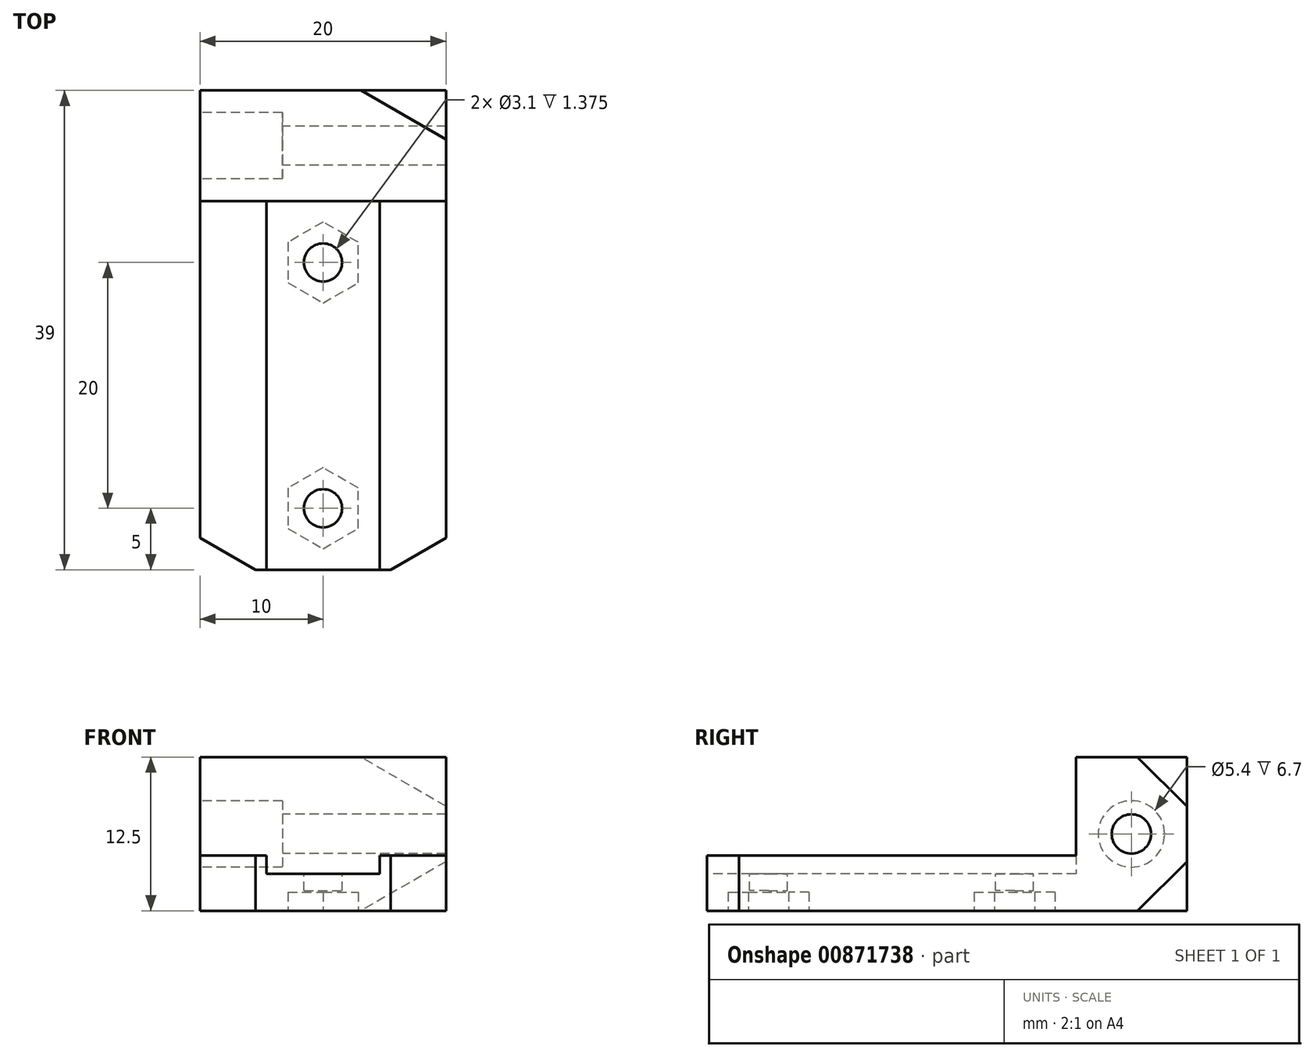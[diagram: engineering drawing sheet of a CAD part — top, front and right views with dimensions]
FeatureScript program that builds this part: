
annotation { "Feature Type Name" : "Feature", "Feature Type Description" : "" }
export const myFeature = defineFeature(function(context is Context, id is Id, definition is map)
    precondition{}
    {
        {
            var Q0;
            Q0=qCreatedBy(makeId("Top.planeOp"),FACE);
            var sketch = newSketch(context, id + "F0", { "sketchPlane" : qUnion([Q0])});
            skLineSegment(sketch, "E0.bottom", {"start": v(10, 19.5) * mm, "end": v(-10, 19.5) * mm});
            skLineSegment(sketch, "E0.top", {"start": v(10, -19.5) * mm, "end": v(-10, -19.5) * mm});
            skLineSegment(sketch, "E0.left", {"start": v(10, 19.5) * mm, "end": v(10, -19.5) * mm});
            skLineSegment(sketch, "E0.right", {"start": v(-10, 19.5) * mm, "end": v(-10, -19.5) * mm});
            skPoint(sketch, "E0.middle", {"position": v(0, 0) * mm});
            skSolve(sketch);
        }
        {
            var Q0;
            Q0=makeQuery(id+"F0.imprint","IMPRINT",FACE,{"disambiguationData":[TD([[makeQuery(id+"F0.imprint","IMPRINT",EDGE,{"derivedFrom":sQuery(id+"F0.wireOp",EDGE,"E0.bottom")}),1.0]])]});
            extrude(context, id + "F1", {"entities" : qUnion([Q0]), "depth" : 3 * mm, "offsetDistance" : 25 * mm});
        }
        {
            var Q0;
            Q0=makeQuery(id+"F1.opExtrude","CAP_FACE",FACE,{"disambiguationData":[OSD([sQuery(id+"F0.wireOp",EDGE,"E0.bottom"),sQuery(id+"F0.wireOp",EDGE,"E0.top"),sQuery(id+"F0.wireOp",EDGE,"E0.left"),sQuery(id+"F0.wireOp",EDGE,"E0.right")])],"isStart":false});
            var sketch = newSketch(context, id + "F2", { "sketchPlane" : qUnion([Q0])});
            skLineSegment(sketch, "E1", {"start": v(-10, -19.5) * mm, "end": v(-4.6, -19.5) * mm});
            skLineSegment(sketch, "E2", {"start": v(-4.6, -19.5) * mm, "end": v(-4.6, 10.5) * mm});
            skLineSegment(sketch, "E3", {"start": v(-4.6, 10.5) * mm, "end": v(4.6, 10.5) * mm});
            skLineSegment(sketch, "E4", {"start": v(4.6, 10.5) * mm, "end": v(4.6, -19.5) * mm});
            skLineSegment(sketch, "E5", {"start": v(4.6, -19.5) * mm, "end": v(10, -19.5) * mm});
            skLineSegment(sketch, "E6", {"start": v(10, -19.5) * mm, "end": v(10, 19.5) * mm});
            skLineSegment(sketch, "E7", {"start": v(10, 19.5) * mm, "end": v(-10, 19.5) * mm});
            skLineSegment(sketch, "E8", {"start": v(-10, 19.5) * mm, "end": v(-10, -19.5) * mm});
            skLineSegment(sketch, "E9", {"start": v(0, 10.5) * mm, "end": v(0, 0) * mm, "construction": true});
            skSolve(sketch);
        }
        {
            var Q0;
            Q0 = qSketchRegion(id + "F2", true);
            extrude(context, id + "F3", {"entities" : qUnion([Q0]), "operationType" : NewBodyOperationType.ADD, "depth" : 1.5 * mm, "offsetDistance" : 25 * mm});
        }
        {
            var Q0;
            Q0=makeQuery(id+"F1.opExtrude","CAP_FACE",FACE,{"disambiguationData":[OSD([sQuery(id+"F0.wireOp",EDGE,"E0.bottom"),sQuery(id+"F0.wireOp",EDGE,"E0.top"),sQuery(id+"F0.wireOp",EDGE,"E0.left"),sQuery(id+"F0.wireOp",EDGE,"E0.right")])],"isStart":false});
            var sketch = newSketch(context, id + "F4", { "sketchPlane" : qUnion([Q0])});
            skLineSegment(sketch, "E10.bottom", {"start": v(-10, 19.5) * mm, "end": v(10, 19.5) * mm});
            skLineSegment(sketch, "E10.top", {"start": v(-10, 10.5) * mm, "end": v(10, 10.5) * mm});
            skLineSegment(sketch, "E10.left", {"start": v(-10, 19.5) * mm, "end": v(-10, 10.5) * mm});
            skLineSegment(sketch, "E10.right", {"start": v(10, 19.5) * mm, "end": v(10, 10.5) * mm});
            skSolve(sketch);
        }
        {
            var Q0;
            Q0 = qSketchRegion(id + "F4", true);
            var Q1;
            Q1=makeQuery(id+"F1.opExtrude","CAP_FACE",FACE,{"disambiguationData":[OSD([sQuery(id+"F0.wireOp",EDGE,"E0.bottom"),sQuery(id+"F0.wireOp",EDGE,"E0.top"),sQuery(id+"F0.wireOp",EDGE,"E0.left"),sQuery(id+"F0.wireOp",EDGE,"E0.right")])],"isStart":false});
            extrude(context, id + "F5", {"entities" : qUnion([Q0]), "operationType" : NewBodyOperationType.ADD, "depth" : 9.5 * mm, "endBoundEntityFace" : qUnion([Q1]), "hasOffset" : true, "offsetDistance" : -10 * mm, "offsetOppositeDirection" : true});
        }
        {
            var Q0;
            Q0=makeQuery(id+"F5.boolean.opBoolean","MERGE",FACE,{"derivedFrom":[makeQuery(id+"F3.boolean.opBoolean","MERGE",FACE,{"derivedFrom":[makeQuery(id+"F1.opExtrude","SWEPT_FACE",FACE,{"disambiguationData":[OSD([sQuery(id+"F0.wireOp",EDGE,"E0.right")])]}),makeQuery(id+"F3.opExtrude","SWEPT_FACE",FACE,{"disambiguationData":[OSD([sQuery(id+"F2.wireOp",EDGE,"E8")])]})]}),makeQuery(id+"F5.opExtrude","SWEPT_FACE",FACE,{"disambiguationData":[OSD([sQuery(id+"F4.wireOp",EDGE,"E10.left")])]})]});
            var sketch = newSketch(context, id + "F6", { "sketchPlane" : qUnion([Q0])});
            skCircle(sketch, "E11", {"center": v(-15, 6.25) * mm, "radius": 1.6 * mm});
            skLineSegment(sketch, "E12", {"start": v(-15, 6.25) * mm, "end": v(-15, 12.5) * mm, "construction": true});
            skLineSegment(sketch, "E13", {"start": v(-15, 6.25) * mm, "end": v(-15, 3) * mm, "construction": true});
            skLineSegment(sketch, "E14", {"start": v(-15, 6.25) * mm, "end": v(-19.5, 6.25) * mm, "construction": true});
            skSolve(sketch);
        }
        {
            var Q0;
            Q0 = qSketchRegion(id + "F6", true);
            extrude(context, id + "F7", {"entities" : qUnion([Q0]), "operationType" : NewBodyOperationType.REMOVE, "endBound" : BoundingType.THROUGH_ALL, "oppositeDirection" : true, "depth" : 25 * mm, "offsetDistance" : 25 * mm});
        }
        {
            var Q0;
            Q0=makeQuery(id+"F1.opExtrude","CAP_FACE",FACE,{"disambiguationData":[OSD([sQuery(id+"F0.wireOp",EDGE,"E0.bottom"),sQuery(id+"F0.wireOp",EDGE,"E0.top"),sQuery(id+"F0.wireOp",EDGE,"E0.left"),sQuery(id+"F0.wireOp",EDGE,"E0.right")])],"isStart":false});
            var sketch = newSketch(context, id + "F8", { "sketchPlane" : qUnion([Q0])});
            skLineSegment(sketch, "E15", {"start": v(0, 5.5) * mm, "end": v(0, 5.5) * mm});
            skLineSegment(sketch, "E16", {"start": v(0, -14.5) * mm, "end": v(0, -14.5) * mm});
            skArc(sketch, "E17.0.startCap", {"start": v(-1.55, 5.5) * mm, "mid": v(0, 7.05) * mm, "end": v(1.55, 5.5) * mm});
            skArc(sketch, "E17.0.endCap", {"start": v(1.55, 5.5) * mm, "mid": v(0, 3.95) * mm, "end": v(-1.55, 5.5) * mm});
            skLineSegment(sketch, "E17.0.left", {"start": v(1.55, 5.5) * mm, "end": v(1.55, 5.5) * mm});
            skLineSegment(sketch, "E17.0.right", {"start": v(-1.55, 5.5) * mm, "end": v(-1.55, 5.5) * mm});
            skArc(sketch, "E17.1.startCap", {"start": v(-1.55, -14.5) * mm, "mid": v(0, -12.95) * mm, "end": v(1.55, -14.5) * mm});
            skArc(sketch, "E17.1.endCap", {"start": v(1.55, -14.5) * mm, "mid": v(0, -16.05) * mm, "end": v(-1.55, -14.5) * mm});
            skLineSegment(sketch, "E17.1.left", {"start": v(1.55, -14.5) * mm, "end": v(1.55, -14.5) * mm});
            skLineSegment(sketch, "E17.1.right", {"start": v(-1.55, -14.5) * mm, "end": v(-1.55, -14.5) * mm});
            skSolve(sketch);
        }
        {
            var Q0;
            Q0 = qSketchRegion(id + "F8", true);
            extrude(context, id + "F9", {"entities" : qUnion([Q0]), "operationType" : NewBodyOperationType.REMOVE, "endBound" : BoundingType.UP_TO_NEXT, "oppositeDirection" : true, "depth" : 25 * mm, "offsetDistance" : 25 * mm});
        }
        {
            var Q0;
            Q0=makeQuery(id+"F1.opExtrude","CAP_FACE",FACE,{"disambiguationData":[OSD([sQuery(id+"F0.wireOp",EDGE,"E0.bottom"),sQuery(id+"F0.wireOp",EDGE,"E0.top"),sQuery(id+"F0.wireOp",EDGE,"E0.left"),sQuery(id+"F0.wireOp",EDGE,"E0.right")])],"isStart":true});
            var sketch = newSketch(context, id + "F10", { "sketchPlane" : qUnion([Q0])});
            skCircle(sketch, "E18.cCircle", {"center": v(0, 14.5) * mm, "radius": 2.85 * mm, "construction": true});
            skLineSegment(sketch, "E18.0", {"start": v(2.85, 16.15) * mm, "end": v(2.85, 12.85) * mm});
            skLineSegment(sketch, "E18.1", {"start": v(2.85, 12.85) * mm, "end": v(0, 11.2) * mm});
            skLineSegment(sketch, "E18.2", {"start": v(0, 11.2) * mm, "end": v(-2.85, 12.85) * mm});
            skLineSegment(sketch, "E18.3", {"start": v(-2.85, 12.85) * mm, "end": v(-2.85, 16.15) * mm});
            skLineSegment(sketch, "E18.4", {"start": v(-2.85, 16.15) * mm, "end": v(0, 17.8) * mm});
            skLineSegment(sketch, "E18.5", {"start": v(0, 17.8) * mm, "end": v(2.85, 16.15) * mm});
            skPoint(sketch, "E18.0.midPoint", {"position": v(2.85, 14.5) * mm});
            skCircle(sketch, "E19.cCircle", {"center": v(0, -5.5) * mm, "radius": 2.85 * mm, "construction": true});
            skLineSegment(sketch, "E19.0", {"start": v(2.85, -3.85) * mm, "end": v(2.85, -7.15) * mm});
            skLineSegment(sketch, "E19.1", {"start": v(2.85, -7.15) * mm, "end": v(0, -8.8) * mm});
            skLineSegment(sketch, "E19.2", {"start": v(0, -8.8) * mm, "end": v(-2.85, -7.15) * mm});
            skLineSegment(sketch, "E19.3", {"start": v(-2.85, -7.15) * mm, "end": v(-2.85, -3.85) * mm});
            skLineSegment(sketch, "E19.4", {"start": v(-2.85, -3.85) * mm, "end": v(0, -2.2) * mm});
            skLineSegment(sketch, "E19.5", {"start": v(0, -2.2) * mm, "end": v(2.85, -3.85) * mm});
            skPoint(sketch, "E19.0.midPoint", {"position": v(2.85, -5.5) * mm});
            skSolve(sketch);
        }
        {
            var Q0;
            Q0 = qSketchRegion(id + "F10", true);
            extrude(context, id + "F11", {"entities" : qUnion([Q0]), "operationType" : NewBodyOperationType.REMOVE, "oppositeDirection" : true, "depth" : 1.5 * mm, "offsetDistance" : 25 * mm});
        }
        {
            var Q0;
            Q0=makeQuery(id+"F5.boolean.opBoolean","MERGE",FACE,{"derivedFrom":[makeQuery(id+"F3.boolean.opBoolean","MERGE",FACE,{"derivedFrom":[makeQuery(id+"F1.opExtrude","SWEPT_FACE",FACE,{"disambiguationData":[OSD([sQuery(id+"F0.wireOp",EDGE,"E0.right")])]}),makeQuery(id+"F3.opExtrude","SWEPT_FACE",FACE,{"disambiguationData":[OSD([sQuery(id+"F2.wireOp",EDGE,"E8")])]})]}),makeQuery(id+"F5.opExtrude","SWEPT_FACE",FACE,{"disambiguationData":[OSD([sQuery(id+"F4.wireOp",EDGE,"E10.left")])]})]});
            var sketch = newSketch(context, id + "F12", { "sketchPlane" : qUnion([Q0])});
            skCircle(sketch, "E20", {"center": v(-15, 6.25) * mm, "radius": 2.7 * mm});
            skSolve(sketch);
        }
        {
            var Q0;
            Q0 = qSketchRegion(id + "F12", true);
            var Q1;
            Q1=sQuery(id+"F12.wireOp",EDGE,"E20");
            extrude(context, id + "F13", {"entities" : qUnion([Q0]), "operationType" : NewBodyOperationType.REMOVE, "surfaceEntities" : qUnion([Q1]), "oppositeDirection" : true, "depth" : 6.7 * mm, "offsetDistance" : 25 * mm});
        }
        {
            var Q0;
            Q0=makeQuery(id+"F5.boolean.opBoolean","MERGE",FACE,{"derivedFrom":[makeQuery(id+"F3.boolean.opBoolean","MERGE",FACE,{"derivedFrom":[makeQuery(id+"F1.opExtrude","SWEPT_FACE",FACE,{"disambiguationData":[OSD([sQuery(id+"F0.wireOp",EDGE,"E0.bottom")])]}),makeQuery(id+"F3.opExtrude","SWEPT_FACE",FACE,{"disambiguationData":[OSD([sQuery(id+"F2.wireOp",EDGE,"E7")])]})]}),makeQuery(id+"F5.opExtrude","SWEPT_FACE",FACE,{"disambiguationData":[OSD([sQuery(id+"F4.wireOp",EDGE,"E10.bottom")])]})]});
            var sketch = newSketch(context, id + "F14", { "sketchPlane" : qUnion([Q0])});
            skLineSegment(sketch, "E21", {"start": v(-10, 12.5) * mm, "end": v(-10, 8.5) * mm});
            skLineSegment(sketch, "E22", {"start": v(-10, 8.5) * mm, "end": v(-3.07, 12.5) * mm});
            skLineSegment(sketch, "E23", {"start": v(-3.07, 12.5) * mm, "end": v(-10, 12.5) * mm});
            skLineSegment(sketch, "E24", {"start": v(-10, 4) * mm, "end": v(-3.07, 0) * mm});
            skLineSegment(sketch, "E25", {"start": v(-3.07, 0) * mm, "end": v(-10, 0) * mm});
            skLineSegment(sketch, "E26", {"start": v(-10, 0) * mm, "end": v(-10, 4) * mm});
            skSolve(sketch);
        }
        {
            var Q0;
            Q0=makeQuery(id+"F5.boolean.opBoolean","MERGE",FACE,{"derivedFrom":[makeQuery(id+"F3.boolean.opBoolean","MERGE",FACE,{"derivedFrom":[makeQuery(id+"F1.opExtrude","SWEPT_FACE",FACE,{"disambiguationData":[OSD([sQuery(id+"F0.wireOp",EDGE,"E0.left")])]}),makeQuery(id+"F3.opExtrude","SWEPT_FACE",FACE,{"disambiguationData":[OSD([sQuery(id+"F2.wireOp",EDGE,"E6")])]})]}),makeQuery(id+"F5.opExtrude","SWEPT_FACE",FACE,{"disambiguationData":[OSD([sQuery(id+"F4.wireOp",EDGE,"E10.right")])]})]});
            var sketch = newSketch(context, id + "F15", { "sketchPlane" : qUnion([Q0])});
            skLineSegment(sketch, "E27", {"start": v(19.5, 0) * mm, "end": v(19.5, 4) * mm});
            skLineSegment(sketch, "E28", {"start": v(19.5, 4) * mm, "end": v(15.5, 0) * mm});
            skLineSegment(sketch, "E29", {"start": v(15.5, 0) * mm, "end": v(19.5, 0) * mm});
            skLineSegment(sketch, "E30", {"start": v(19.5, 8.5) * mm, "end": v(19.5, 12.5) * mm});
            skLineSegment(sketch, "E31", {"start": v(19.5, 12.5) * mm, "end": v(15.5, 12.5) * mm});
            skLineSegment(sketch, "E32", {"start": v(15.5, 12.5) * mm, "end": v(19.5, 8.5) * mm});
            skSolve(sketch);
        }
        {
            var Q1;
            Q1=makeQuery(id+"F15.imprint","IMPRINT",FACE,{"disambiguationData":[TD([[makeQuery(id+"F15.imprint","IMPRINT",EDGE,{"derivedFrom":sQuery(id+"F15.wireOp",EDGE,"E27")}),-1.0]])]});
            var Q2;
            Q2=makeQuery(id+"F14.imprint","IMPRINT",FACE,{"disambiguationData":[TD([[makeQuery(id+"F14.imprint","IMPRINT",EDGE,{"derivedFrom":sQuery(id+"F14.wireOp",EDGE,"E24")}),-1.0]])]});
            var Q3;
            Q3=sQuery(id+"F14.wireOp",VERTEX,"E24.end");
            var Q4;
            Q4=sQuery(id+"F15.wireOp",VERTEX,"E28.end");
            loft(context, id + "F16", {"operationType" : NewBodyOperationType.REMOVE, "sheetProfilesArray" : [{ "sheetProfileEntities" : qUnion([Q1]) }, { "sheetProfileEntities" : qUnion([Q2]) }], "matchConnections" : true, "connections" : [{ "connectionEntities" : qUnion([Q3, Q4]), "connectionEdgeQueries" : qUnion([]), "connectionEdgeParameters" : [] }]});
        }
        {
            var Q1;
            Q1=makeQuery(id+"F15.imprint","IMPRINT",FACE,{"disambiguationData":[TD([[makeQuery(id+"F15.imprint","IMPRINT",EDGE,{"derivedFrom":sQuery(id+"F15.wireOp",EDGE,"E30")}),-1.0]])]});
            var Q2;
            Q2=makeQuery(id+"F14.imprint","IMPRINT",FACE,{"disambiguationData":[TD([[makeQuery(id+"F14.imprint","IMPRINT",EDGE,{"derivedFrom":sQuery(id+"F14.wireOp",EDGE,"E21")}),1.0]])]});
            var Q3;
            Q3=sQuery(id+"F14.wireOp",VERTEX,"E22.end");
            var Q4;
            Q4=sQuery(id+"F15.wireOp",VERTEX,"E31.end");
            loft(context, id + "F17", {"operationType" : NewBodyOperationType.REMOVE, "sheetProfilesArray" : [{ "sheetProfileEntities" : qUnion([Q1]) }, { "sheetProfileEntities" : qUnion([Q2]) }], "matchConnections" : true, "connections" : [{ "connectionEntities" : qUnion([Q3, Q4]), "connectionEdgeQueries" : qUnion([]), "connectionEdgeParameters" : [] }]});
        }
        {
            var Q0;
            Q0=makeQuery(id+"F3.boolean.opBoolean","MERGE",EDGE,{"derivedFrom":[makeQuery(id+"F1.opExtrude","SWEPT_EDGE",EDGE,{"disambiguationData":[OSD([sQuery(id+"F0.wireOp",EDGE,"E0.top"),sQuery(id+"F0.wireOp",EDGE,"E0.left")])]}),makeQuery(id+"F3.opExtrude","SWEPT_EDGE",EDGE,{"disambiguationData":[OSD([sQuery(id+"F2.wireOp",EDGE,"E5"),sQuery(id+"F2.wireOp",EDGE,"E6")])]})]});
            var Q1;
            Q1=makeQuery(id+"F3.boolean.opBoolean","MERGE",EDGE,{"derivedFrom":[makeQuery(id+"F1.opExtrude","SWEPT_EDGE",EDGE,{"disambiguationData":[OSD([sQuery(id+"F0.wireOp",EDGE,"E0.top"),sQuery(id+"F0.wireOp",EDGE,"E0.right")])]}),makeQuery(id+"F3.opExtrude","SWEPT_EDGE",EDGE,{"disambiguationData":[OSD([sQuery(id+"F2.wireOp",EDGE,"E1"),sQuery(id+"F2.wireOp",EDGE,"E8")])]})]});
            chamfer(context, id + "F18", {"entities" : qUnion([Q0, Q1]), "chamferType" : ChamferType.OFFSET_ANGLE, "width" : 4.5 * mm, "oppositeDirection" : true, "angle" : 30 * degree, "tangentPropagation" : true});
        }
        {
            var Q0;
            Q0=makeQuery(id+"F11.boolean.opBoolean","COPY",FACE,{"derivedFrom":makeQuery(id+"F11.opExtrude","CAP_FACE",FACE,{"disambiguationData":[OSD([sQuery(id+"F10.wireOp",EDGE,"E18.0"),sQuery(id+"F10.wireOp",EDGE,"E18.1"),sQuery(id+"F10.wireOp",EDGE,"E18.2"),sQuery(id+"F10.wireOp",EDGE,"E18.3"),sQuery(id+"F10.wireOp",EDGE,"E18.4"),sQuery(id+"F10.wireOp",EDGE,"E18.5")])],"isStart":false})});
            var sketch = newSketch(context, id + "F19", { "sketchPlane" : qUnion([Q0])});
            skCircle(sketch, "E33.0", {"center": v(0, 14.5) * mm, "radius": 1.55 * mm});
            skCircle(sketch, "E33.1", {"center": v(0, -5.5) * mm, "radius": 1.55 * mm});
            skSolve(sketch);
        }
        {
            var Q0;
            Q0 = qSketchRegion(id + "F19", true);
            extrude(context, id + "F20", {"entities" : qUnion([Q0]), "operationType" : NewBodyOperationType.ADD, "oppositeDirection" : true, "depth" : .125 * mm, "offsetDistance" : 25 * mm});
        }
    });
